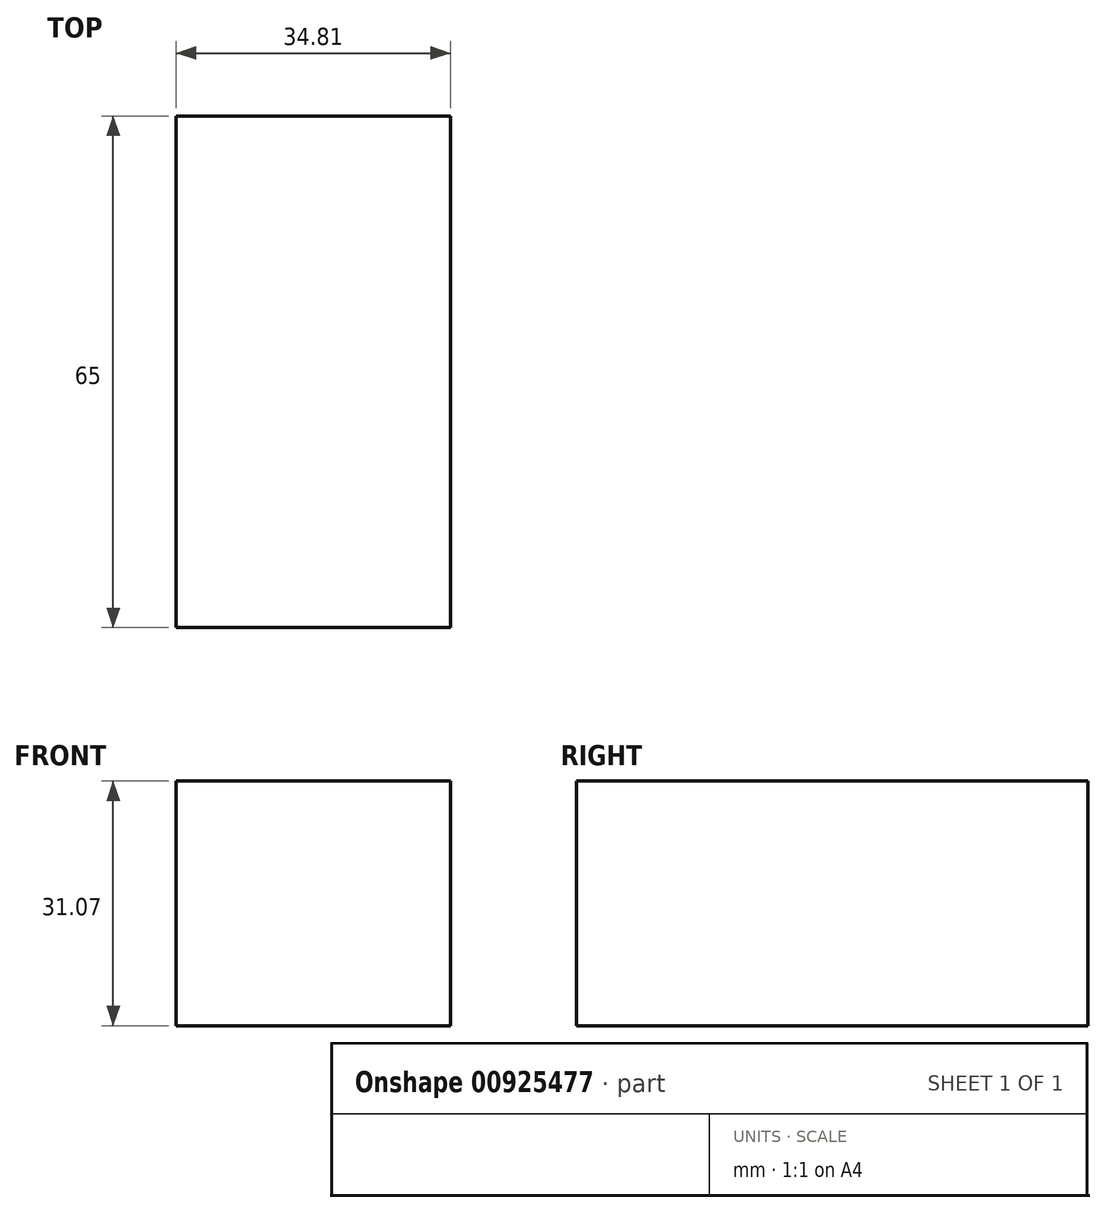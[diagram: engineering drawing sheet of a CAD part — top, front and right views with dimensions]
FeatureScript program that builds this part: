
annotation { "Feature Type Name" : "Feature", "Feature Type Description" : "" }
export const myFeature = defineFeature(function(context is Context, id is Id, definition is map)
    precondition{}
    {
        {
            var Q0;
            Q0=qCreatedBy(makeId("Front.planeOp"),FACE);
            var sketch = newSketch(context, id + "F0", { "sketchPlane" : qUnion([Q0])});
            skLineSegment(sketch, "E0.bottom", {"start": v(-17.79, 21.73) * mm, "end": v(17.02, 21.73) * mm});
            skLineSegment(sketch, "E0.top", {"start": v(-17.79, -24.62) * mm, "end": v(17.02, -24.62) * mm});
            skLineSegment(sketch, "E0.left", {"start": v(-17.79, 21.73) * mm, "end": v(-17.79, -24.62) * mm});
            skLineSegment(sketch, "E0.right", {"start": v(17.02, 21.73) * mm, "end": v(17.02, -24.62) * mm});
            skLineSegment(sketch, "E1.top", {"start": v(-17.79, -60.95) * mm, "end": v(17.02, -60.95) * mm});
            skLineSegment(sketch, "E1.left", {"start": v(-17.79, -24.62) * mm, "end": v(-17.79, -60.95) * mm});
            skLineSegment(sketch, "E1.right", {"start": v(17.02, -24.62) * mm, "end": v(17.02, -60.95) * mm});
            skLineSegment(sketch, "E2", {"start": v(-17.79, -55.7) * mm, "end": v(17.02, -55.7) * mm});
            skCircle(sketch, "E3", {"center": v(0, -5.57) * mm, "radius": 11.86 * mm});
            skLineSegment(sketch, "E4.bottom", {"start": v(-3.67, 20.2) * mm, "end": v(4.21, 20.2) * mm});
            skLineSegment(sketch, "E4.top", {"start": v(-3.67, 7.9) * mm, "end": v(4.21, 7.9) * mm});
            skLineSegment(sketch, "E4.left", {"start": v(-3.67, 20.2) * mm, "end": v(-3.67, 7.9) * mm});
            skLineSegment(sketch, "E4.right", {"start": v(4.21, 20.2) * mm, "end": v(4.21, 7.9) * mm});
            skSolve(sketch);
        }
        {
            var Q0;
            {var subQ0=sQuery(id+"F0.wireOp",EDGE,"E0.top");Q0=makeQuery(id+"F0.imprint","IMPRINT",FACE,{"disambiguationData":[TD([[makeQuery(id+"F0.imprint","IMPRINT",EDGE,{"derivedFrom":subQ0}),-1.0]])]});}
            extrude(context, id + "F1", {"entities" : qUnion([Q0]), "depth" : 40 * mm, "offsetDistance" : 25 * mm});
        }
        {
            var Q0;
            Q0=makeQuery(id+"F1.opExtrude","CAP_FACE",FACE,{"disambiguationData":[OSD([sQuery(id+"F0.wireOp",EDGE,"E0.top"),sQuery(id+"F0.wireOp",EDGE,"E1.left"),sQuery(id+"F0.wireOp",EDGE,"E1.right"),sQuery(id+"F0.wireOp",EDGE,"E2")])],"isStart":false});
            extrude(context, id + "F2", {"entities" : qUnion([Q0]), "operationType" : NewBodyOperationType.ADD, "depth" : 25 * mm, "offsetDistance" : 25 * mm});
        }
    });
